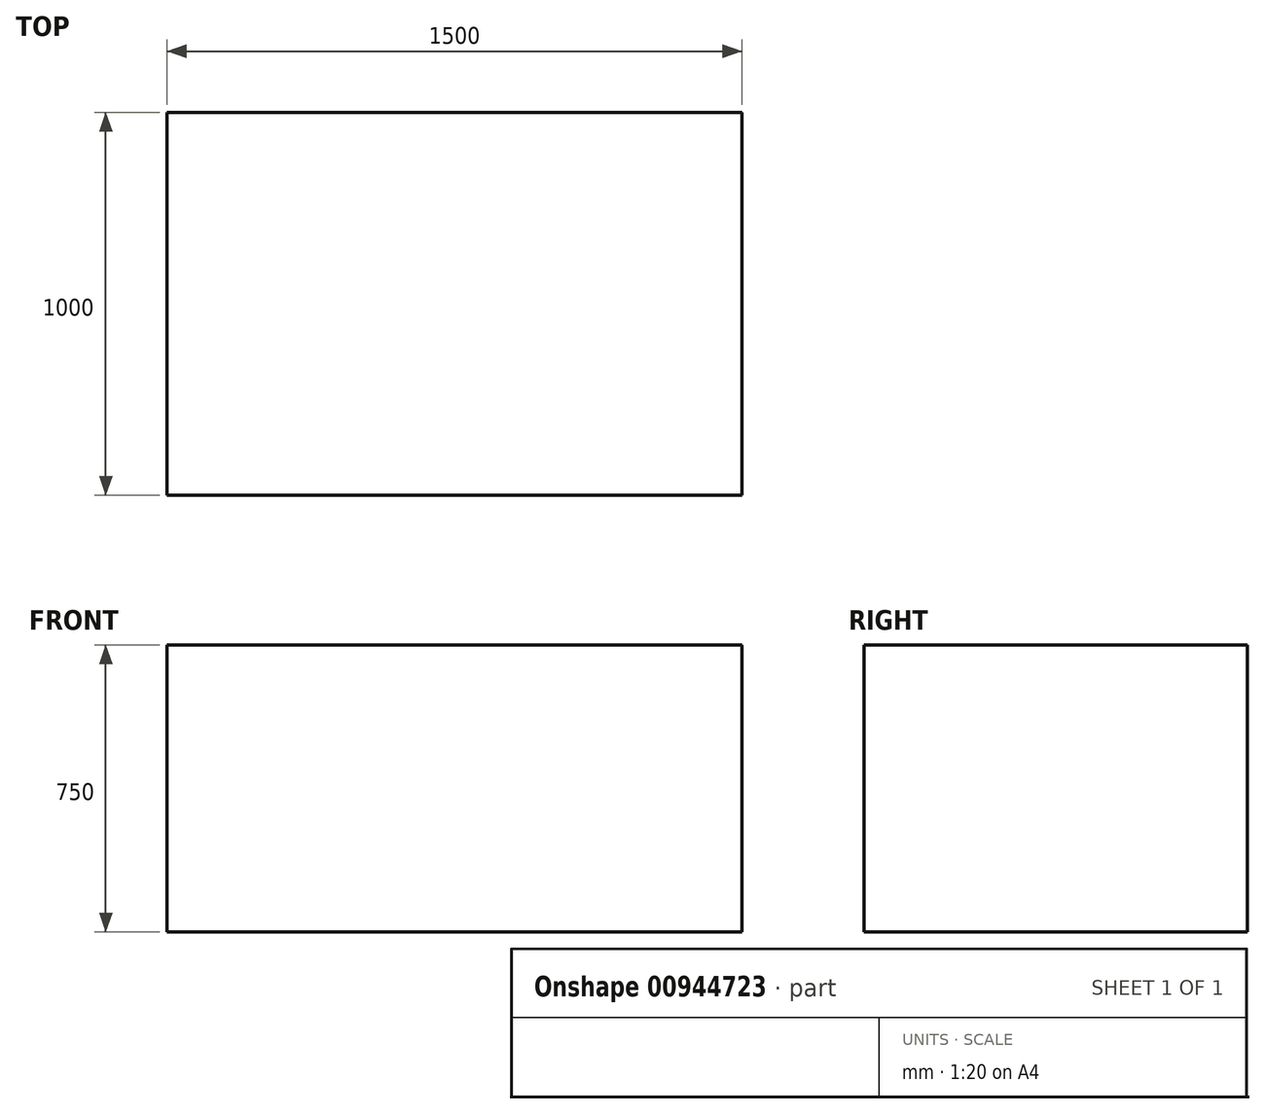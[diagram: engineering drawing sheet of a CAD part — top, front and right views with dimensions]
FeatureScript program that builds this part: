
annotation { "Feature Type Name" : "Feature", "Feature Type Description" : "" }
export const myFeature = defineFeature(function(context is Context, id is Id, definition is map)
    precondition{}
    {
        {
            var Q0;
            Q0=qCreatedBy(makeId("Top.planeOp"),FACE);
            var sketch = newSketch(context, id + "F0", { "sketchPlane" : qUnion([Q0])});
            skLineSegment(sketch, "E0.bottom", {"start": v(0, 0) * mm, "end": v(1500, 0) * mm});
            skLineSegment(sketch, "E0.top", {"start": v(0, -1000) * mm, "end": v(1500, -1000) * mm});
            skLineSegment(sketch, "E0.left", {"start": v(0, 0) * mm, "end": v(0, -1000) * mm});
            skLineSegment(sketch, "E0.right", {"start": v(1500, 0) * mm, "end": v(1500, -1000) * mm});
            skSolve(sketch);
        }
        {
            var Q0;
            Q0=makeQuery(id+"F0.imprint","IMPRINT",FACE,{"disambiguationData":[TD([[makeQuery(id+"F0.imprint","IMPRINT",EDGE,{"derivedFrom":sQuery(id+"F0.wireOp",EDGE,"E0.bottom")}),-1.0]])]});
            extrude(context, id + "F1", {"entities" : qUnion([Q0]), "depth" : 750 * mm, "offsetDistance" : 25 * mm});
        }
    });
